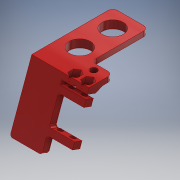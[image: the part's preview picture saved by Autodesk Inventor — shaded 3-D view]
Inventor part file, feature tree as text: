
AUTODESK INVENTOR PART (.ipt)
format: ipt  version: 2018.3 (Build 223284000, 284)  size: 546,816 bytes
history: native  units: mm
features: extrude x21, sketch x20, fillet x11, chamfer x3, projected_geometry x2, draft x1, plane x1
ambient origin geometry x8: Origin, YZ Plane, XZ Plane, XY Plane, X Axis, Y Axis, Z Axis, Center Point
bodies: Solid1 (feature_tree)
feature tree (59):
  extrude  "Extrusion1"  Depth=65.0mm
  sketch  "Sketch2"  dims[d2=4.0mm d3=0.0mm d4=16.5mm]
  extrude  "Extrusion5"  Depth=16.5mm
  extrude  "Extrusion8"  Depth=14.0mm
  fillet  "Fillet4"  Radius=14.0mm
  extrude  "Extrusion9"  Depth=4.0mm
  extrude  "Extrusion11"  Depth=4.0mm
  extrude  "Extrusion17"  TaperAngle=0.0deg  [1 undecoded]
  fillet  "Fillet10"  Radius=4.0mm
  extrude  "Extrusion20"  Depth=22.0mm
  extrude  "Extrusion21"  Depth=1.0mm
  extrude  "Extrusion23"  Depth=5.4mm
  extrude  "Extrusion25"  Depth=10.0mm TaperAngle=0.0deg
  extrude  "Extrusion29"  Depth=1.5mm
  extrude  "Extrusion30"  Depth=1.5mm
  extrude  "Extrusion31"  Depth=3.0mm TaperAngle=0.0deg
  fillet  "Fillet16"  Radius=0.5mm
  fillet  "Fillet18"  Radius=46.0mm
  extrude  "Extrusion32"  Depth=7.0mm
  chamfer  "Chamfer3"  Distance=25.0mm
  extrude  "Extrusion33"  Depth=25.0mm TaperAngle=0.0deg
  chamfer  "Chamfer4"  Distance=25.0mm
  fillet  "Fillet19"  Radius=1.5mm
  extrude  "Extrusion34"  Depth=5.0mm
  fillet  "Fillet20"  Radius=5.0mm
  draft  "FaceDraft1"
  chamfer  "Chamfer6"  Distance=3.0mm
  fillet  "Fillet21"  Radius=20.0mm
  extrude  "Extrusion35"  Depth=3.0mm TaperAngle=0.0deg
  extrude  "Extrusion42"  Depth=5.0mm
  fillet  "Fillet27"  Radius=29.0mm
  plane  "Work Plane6"
  sketch  "Sketch37"  dims[d141=1.0mm d142=0.0mm d161=5.0mm d165=5.0mm]
  extrude  "Extrusion43"  Depth=3.0mm TaperAngle=0.0deg
  extrude  "Extrusion44"  Depth=1.0mm
  extrude  "Extrusion45"  Depth=2.0mm
  fillet  "Fillet28"  Radius=19.5mm
  fillet  "Fillet29"  Radius=37.5mm
  fillet  "Fillet30"  Radius=7.5mm
  sketch  "Sketch1"  dims[d0=45.0mm d1=65.0mm]
  sketch  "Sketch4"  dims[d5=16.5mm d6=14.0mm d7=14.0mm]
  sketch  "Sketch6"  dims[d8=25.883mm d20=4.0mm]
  sketch  "Sketch8"  dims[d21=5.0mm d22=4.0mm]
  sketch  "Sketch13"  dims[d24=10.0mm d25=0.0mm d26=0.0mm d27=4.0mm]
  sketch  "Sketch16"  dims[d34=22.0mm d35=22.0mm]
  sketch  "Sketch17"  dims[d36=3.0mm d37=0.0mm d38=1.0mm]
  sketch  "Sketch19"  dims[d39=3.0mm d40=0.0mm d47=5.4mm]
  sketch  "Sketch20"  dims[d48=10.0mm d52=10.0mm d53=0.0mm]
  sketch  "Sketch23"  dims[d88=5.0mm d89=1.5mm]
  sketch  "Sketch24"  dims[d91=5.0mm d92=1.5mm]
  sketch  "Sketch25"  dims[d93=3.25mm d94=3.0mm d95=0.0mm d106=0.5mm d114=46.0mm]
  sketch  "Sketch26"  dims[d115=27.925268mm d116=7.0mm]
  sketch  "Sketch28"  dims[d117=19.198622mm]
  sketch  "Sketch29"  dims[d118=3.490659mm d119=25.0mm d120=0.0mm]
  sketch  "Sketch30"  dims[d123=3.490659mm d124=25.0mm d125=0.0mm]
  projected_geometry  "Projected Loop1"
  projected_geometry  "Projected Loop2"
  sketch  "Sketch36"  dims[d135=10.0mm d136=25.0mm d137=0.0mm d140=1.5mm]
  sketch  "Sketch38"  dims[d167=7.0mm d168=3.0mm d169=20.0mm d170=0.0mm d172=3.0mm d173=0.0mm d174=5.0mm d175=29.0mm d176=3.0mm d177=0.0mm d178=1.0mm d180=2.0mm d181=19.5mm d182=37.5mm d184=7.5mm d185=4.0mm d186=0.0mm d187=4.0mm d188=2.5mm d189=45.0deg d190=1.0mm d191=30.0mm d192=0.5mm d194=90.0deg d195=1.25mm d196=15.0mm d197=3.0mm d198=1.0mm d199=1.0mm d200=0.0mm d201=1.0mm d202=2.5mm d203=45.0deg d204=2.0mm d208=1.5mm d209=5.0mm d210=1.0mm d211=0.0mm d212=0.5mm d213=6.981317mm d214=2.5mm d215=4.5mm d216=30.0deg d217=2.0mm d218=1.0mm d219=0.0mm d242=15.0mm d260=17.0mm d261=45.0mm d262=10.0mm d263=0.0mm d264=4.0mm d265=-5.0mm d266=7.5mm d267=2.0mm d268=90.0deg d269=10.0mm d270=0.0mm d271=3.5mm d272=0.0mm d273=4.5mm d274=22.0mm d275=0.0mm d276=5.0mm d277=5.0mm d278=2.0mm]
note: 1 required parameter value undecoded (feature->parameter linkage not recoverable at this tier; creation-order binding heuristic only, values carry confidence <= 0.55)
